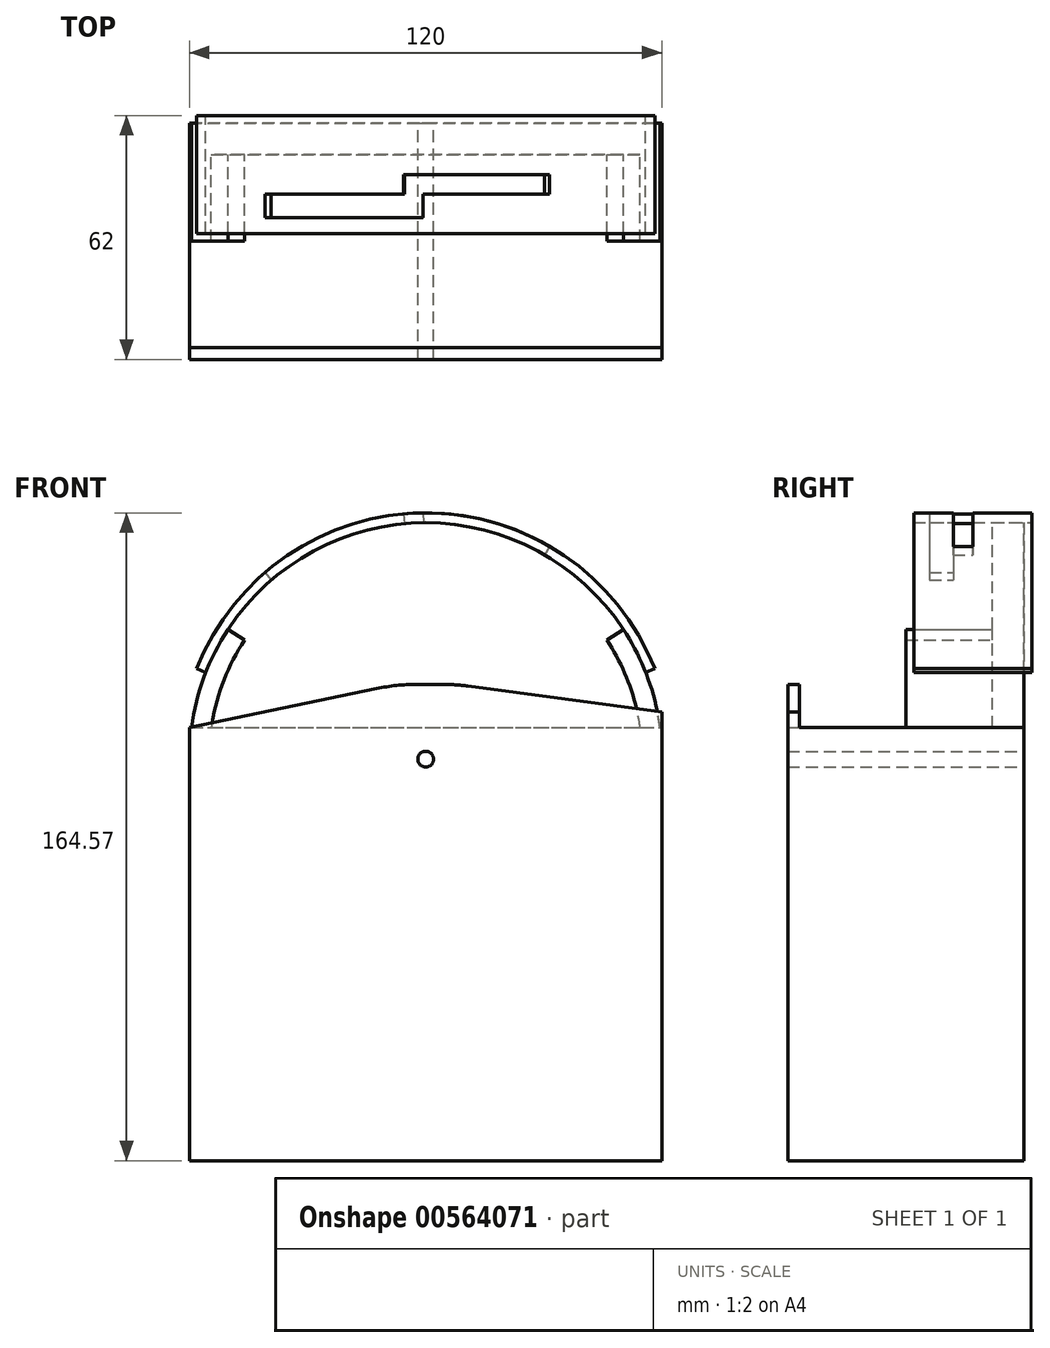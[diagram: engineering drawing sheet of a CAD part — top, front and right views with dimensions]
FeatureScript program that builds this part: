
annotation { "Feature Type Name" : "Feature", "Feature Type Description" : "" }
export const myFeature = defineFeature(function(context is Context, id is Id, definition is map)
    precondition{}
    {
        {
            var Q0;
            Q0=qCreatedBy(makeId("Front.planeOp"),FACE);
            var sketch = newSketch(context, id + "F0", { "sketchPlane" : qUnion([Q0])});
            skLineSegment(sketch, "E0.bottom", {"start": v(-60, 8) * mm, "end": v(60, 8) * mm});
            skLineSegment(sketch, "E0.top", {"start": v(-60, -102) * mm, "end": v(60, -102) * mm});
            skLineSegment(sketch, "E0.left", {"start": v(-60, 8) * mm, "end": v(-60, -102) * mm});
            skLineSegment(sketch, "E0.right", {"start": v(60, 8) * mm, "end": v(60, -102) * mm});
            skLineSegment(sketch, "E1", {"start": v(-60, 3) * mm, "end": v(60, 3) * mm});
            skArc(sketch, "E2", {"start": v(60.07, 0) * mm, "mid": v(0, 60.07) * mm, "end": v(-60.07, 0) * mm});
            skArc(sketch, "E3", {"start": v(55.07, 0) * mm, "mid": v(0, 55.07) * mm, "end": v(-55.07, 0) * mm});
            skArc(sketch, "E4", {"start": v(62.57, 0) * mm, "mid": v(0, 62.57) * mm, "end": v(-62.57, 0) * mm});
            skLineSegment(sketch, "E5", {"start": v(0, 0) * mm, "end": v(-50.2, 33) * mm, "construction": true});
            skLineSegment(sketch, "E6", {"start": v(0, 0) * mm, "end": v(50.2, 33) * mm, "construction": true});
            skLineSegment(sketch, "E7", {"start": v(0, 0) * mm, "end": v(-58.2, 23) * mm, "construction": true});
            skLineSegment(sketch, "E8", {"start": v(0, 0) * mm, "end": v(58.2, 23) * mm, "construction": true});
            skLineSegment(sketch, "E9", {"start": v(0, 0) * mm, "end": v(-40.86, 47.39) * mm, "construction": true});
            skLineSegment(sketch, "E10", {"start": v(0, 0) * mm, "end": v(-5.63, 62.32) * mm, "construction": true});
            skLineSegment(sketch, "E11", {"start": v(0, 0) * mm, "end": v(-0.63, 62.57) * mm, "construction": true});
            skLineSegment(sketch, "E12", {"start": v(0, 0) * mm, "end": v(31.46, 54.09) * mm, "construction": true});
            skLineSegment(sketch, "E13", {"start": v(-58.2, 23) * mm, "end": v(-55.87, 22.08) * mm});
            skLineSegment(sketch, "E14", {"start": v(-50.2, 33) * mm, "end": v(-46.02, 30.25) * mm});
            skLineSegment(sketch, "E15", {"start": v(-40.86, 47.39) * mm, "end": v(-39.23, 45.5) * mm});
            skLineSegment(sketch, "E16", {"start": v(-5.63, 62.32) * mm, "end": v(-5.4, 59.83) * mm});
            skLineSegment(sketch, "E17", {"start": v(-0.63, 62.57) * mm, "end": v(-0.6, 60.07) * mm});
            skLineSegment(sketch, "E18", {"start": v(31.46, 54.09) * mm, "end": v(30.2, 51.93) * mm});
            skLineSegment(sketch, "E19", {"start": v(58.2, 23) * mm, "end": v(55.87, 22.08) * mm});
            skLineSegment(sketch, "E20", {"start": v(50.2, 33) * mm, "end": v(46.02, 30.25) * mm});
            skLineSegment(sketch, "E21", {"start": v(0, 0) * mm, "end": v(-40.78, 47.46) * mm, "construction": true});
            skLineSegment(sketch, "E22", {"start": v(0, 0) * mm, "end": v(-32.85, 53.26) * mm, "construction": true});
            skLineSegment(sketch, "E23", {"start": v(0, 0) * mm, "end": v(-27.84, 56.04) * mm, "construction": true});
            skLineSegment(sketch, "E24", {"start": v(0, 0) * mm, "end": v(-3.13, 62.5) * mm, "construction": true});
            skLineSegment(sketch, "E25", {"start": v(0, 0) * mm, "end": v(1.45, -28.96) * mm, "construction": true});
            skLineSegment(sketch, "E26", {"start": v(0, 0) * mm, "end": v(15.23, -24.68) * mm, "construction": true});
            skLineSegment(sketch, "E27", {"start": v(0, 0) * mm, "end": v(12.9, -25.97) * mm, "construction": true});
            skCircle(sketch, "E28", {"center": v(0, 0) * mm, "radius": 29 * mm, "construction": true});
            skSolve(sketch);
        }
        {
            var Q0;
            {var subQ6=sQuery(id+"F0.wireOp",EDGE,"E0.top");Q0=makeQuery(id+"F0.imprint","IMPRINT",FACE,{"disambiguationData":[TD([[makeQuery(id+"F0.imprint","IMPRINT",EDGE,{"derivedFrom":subQ6}),1.0]])]});}
            extrude(context, id + "F1", {"entities" : qUnion([Q0]), "depth" : 60 * mm, "offsetDistance" : 25 * mm});
        }
        {
            var Q0;
            {var subQ0=sQuery(id+"F0.wireOp",EDGE,"E3");var subQ1=sQuery(id+"F0.wireOp",EDGE,"E0.bottom");var subQ2=makeQuery(id+"F0.imprint","INTERSECT",VERTEX,{"disambiguationData":[OD(0.0)],"derivedFrom":[subQ1,subQ0]});Q0=makeQuery(id+"F0.imprint","IMPRINT",FACE,{"disambiguationData":[TD([[makeQuery(id+"F0.imprint","IMPRINT",EDGE,{"disambiguationData":[TD([[subQ2,-1.0]])],"derivedFrom":subQ1}),-1.0]])]});}
            var Q1;
            {var subQ0=sQuery(id+"F0.wireOp",EDGE,"E2");var subQ1=sQuery(id+"F0.wireOp",EDGE,"E0.bottom");var subQ2=makeQuery(id+"F0.imprint","INTERSECT",VERTEX,{"derivedFrom":[subQ1,subQ0]});Q1=makeQuery(id+"F0.imprint","IMPRINT",FACE,{"disambiguationData":[TD([[makeQuery(id+"F0.imprint","IMPRINT",EDGE,{"disambiguationData":[TD([[subQ2,1.0]])],"derivedFrom":subQ1}),-1.0]])]});}
            var Q2;
            {var subQ0=sQuery(id+"F0.wireOp",EDGE,"E0.right");var subQ1=sQuery(id+"F0.wireOp",EDGE,"E0.bottom");var subQ2=makeQuery(id+"F0.imprint","INTERSECT",VERTEX,{"derivedFrom":[subQ1,subQ0]});Q2=makeQuery(id+"F0.imprint","IMPRINT",FACE,{"disambiguationData":[TD([[makeQuery(id+"F0.imprint","IMPRINT",EDGE,{"disambiguationData":[TD([[subQ2,1.0]])],"derivedFrom":subQ1}),-1.0]])]});}
            var Q3;
            {var subQ0=sQuery(id+"F0.wireOp",EDGE,"E1");var subQ3=sQuery(id+"F0.wireOp",EDGE,"E3");var subQ5=makeQuery(id+"F0.imprint","INTERSECT",VERTEX,{"disambiguationData":[OD(0.0)],"derivedFrom":[subQ0,subQ3]});Q3=makeQuery(id+"F0.imprint","IMPRINT",FACE,{"disambiguationData":[TD([[makeQuery(id+"F0.imprint","IMPRINT",EDGE,{"disambiguationData":[TD([[subQ5,1.0]])],"derivedFrom":subQ3}),-1.0]])]});}
            var Q4;
            {var subQ0=sQuery(id+"F0.wireOp",EDGE,"E2");var subQ1=sQuery(id+"F0.wireOp",EDGE,"E0.bottom");var subQ2=makeQuery(id+"F0.imprint","INTERSECT",VERTEX,{"disambiguationData":[OD(1.0)],"derivedFrom":[subQ1,subQ0]});Q4=makeQuery(id+"F0.imprint","IMPRINT",FACE,{"disambiguationData":[TD([[makeQuery(id+"F0.imprint","IMPRINT",EDGE,{"disambiguationData":[TD([[subQ2,1.0]])],"derivedFrom":subQ1}),-1.0]])]});}
            extrude(context, id + "F2", {"entities" : qUnion([Q0, Q1, Q2, Q3, Q4]), "operationType" : NewBodyOperationType.ADD, "depth" : 60 * mm, "offsetDistance" : 25 * mm});
        }
        {
            var Q0;
            {var subQ0=sQuery(id+"F0.wireOp",EDGE,"E3");var subQ1=sQuery(id+"F0.wireOp",EDGE,"E0.bottom");var subQ2=makeQuery(id+"F0.imprint","INTERSECT",VERTEX,{"disambiguationData":[OD(0.0)],"derivedFrom":[subQ1,subQ0]});Q0=makeQuery(id+"F0.imprint","IMPRINT",FACE,{"disambiguationData":[TD([[makeQuery(id+"F0.imprint","IMPRINT",EDGE,{"disambiguationData":[TD([[subQ2,-1.0]])],"derivedFrom":subQ1}),-1.0]])]});}
            var Q1;
            {var subQ0=sQuery(id+"F0.wireOp",EDGE,"E2");var subQ1=sQuery(id+"F0.wireOp",EDGE,"E0.bottom");var subQ2=makeQuery(id+"F0.imprint","INTERSECT",VERTEX,{"derivedFrom":[subQ1,subQ0]});Q1=makeQuery(id+"F0.imprint","IMPRINT",FACE,{"disambiguationData":[TD([[makeQuery(id+"F0.imprint","IMPRINT",EDGE,{"disambiguationData":[TD([[subQ2,1.0]])],"derivedFrom":subQ1}),-1.0]])]});}
            var Q2;
            {var subQ0=sQuery(id+"F0.wireOp",EDGE,"E3");var subQ1=sQuery(id+"F0.wireOp",EDGE,"E0.bottom");var subQ2=makeQuery(id+"F0.imprint","INTERSECT",VERTEX,{"disambiguationData":[OD(0.0)],"derivedFrom":[subQ1,subQ0]});Q2=makeQuery(id+"F0.imprint","IMPRINT",FACE,{"disambiguationData":[TD([[makeQuery(id+"F0.imprint","IMPRINT",EDGE,{"disambiguationData":[TD([[subQ2,-1.0]])],"derivedFrom":subQ1}),1.0]])]});}
            var Q3;
            {var subQ2=sQuery(id+"F0.wireOp",EDGE,"E20");Q3=makeQuery(id+"F0.imprint","IMPRINT",FACE,{"disambiguationData":[TD([[makeQuery(id+"F0.imprint","IMPRINT",EDGE,{"derivedFrom":subQ2}),1.0]])]});}
            var Q4;
            {var subQ6=sQuery(id+"F0.wireOp",EDGE,"E14");Q4=makeQuery(id+"F0.imprint","IMPRINT",FACE,{"disambiguationData":[TD([[makeQuery(id+"F0.imprint","IMPRINT",EDGE,{"derivedFrom":subQ6}),1.0]])]});}
            var Q5;
            {var subQ0=sQuery(id+"F0.wireOp",EDGE,"E14");Q5=makeQuery(id+"F0.imprint","IMPRINT",FACE,{"disambiguationData":[TD([[makeQuery(id+"F0.imprint","IMPRINT",EDGE,{"derivedFrom":subQ0}),-1.0]])]});}
            var Q6;
            {var subQ0=sQuery(id+"F0.wireOp",EDGE,"E1");var subQ3=sQuery(id+"F0.wireOp",EDGE,"E3");var subQ5=makeQuery(id+"F0.imprint","INTERSECT",VERTEX,{"disambiguationData":[OD(0.0)],"derivedFrom":[subQ0,subQ3]});Q6=makeQuery(id+"F0.imprint","IMPRINT",FACE,{"disambiguationData":[TD([[makeQuery(id+"F0.imprint","IMPRINT",EDGE,{"disambiguationData":[TD([[subQ5,1.0]])],"derivedFrom":subQ3}),-1.0]])]});}
            var Q7;
            {var subQ0=sQuery(id+"F0.wireOp",EDGE,"E2");var subQ1=sQuery(id+"F0.wireOp",EDGE,"E0.bottom");var subQ2=makeQuery(id+"F0.imprint","INTERSECT",VERTEX,{"disambiguationData":[OD(1.0)],"derivedFrom":[subQ1,subQ0]});Q7=makeQuery(id+"F0.imprint","IMPRINT",FACE,{"disambiguationData":[TD([[makeQuery(id+"F0.imprint","IMPRINT",EDGE,{"disambiguationData":[TD([[subQ2,1.0]])],"derivedFrom":subQ1}),-1.0]])]});}
            extrude(context, id + "F3", {"entities" : qUnion([Q0, Q1, Q2, Q3, Q4, Q5, Q6, Q7]), "operationType" : NewBodyOperationType.ADD, "depth" : 8 * mm, "offsetDistance" : 25 * mm});
        }
        {
            var Q0;
            {var subQ0=sQuery(id+"F0.wireOp",EDGE,"E14");Q0=makeQuery(id+"F0.imprint","IMPRINT",FACE,{"disambiguationData":[TD([[makeQuery(id+"F0.imprint","IMPRINT",EDGE,{"derivedFrom":subQ0}),-1.0]])]});}
            var Q1;
            {var subQ2=sQuery(id+"F0.wireOp",EDGE,"E20");Q1=makeQuery(id+"F0.imprint","IMPRINT",FACE,{"disambiguationData":[TD([[makeQuery(id+"F0.imprint","IMPRINT",EDGE,{"derivedFrom":subQ2}),1.0]])]});}
            var Q2;
            {var subQ0=sQuery(id+"F0.wireOp",EDGE,"E2");var subQ1=sQuery(id+"F0.wireOp",EDGE,"E0.bottom");var subQ2=makeQuery(id+"F0.imprint","INTERSECT",VERTEX,{"derivedFrom":[subQ1,subQ0]});Q2=makeQuery(id+"F0.imprint","IMPRINT",FACE,{"disambiguationData":[TD([[makeQuery(id+"F0.imprint","IMPRINT",EDGE,{"disambiguationData":[TD([[subQ2,1.0]])],"derivedFrom":subQ1}),-1.0]])]});}
            var Q3;
            {var subQ0=sQuery(id+"F0.wireOp",EDGE,"E1");var subQ3=sQuery(id+"F0.wireOp",EDGE,"E3");var subQ5=makeQuery(id+"F0.imprint","INTERSECT",VERTEX,{"disambiguationData":[OD(0.0)],"derivedFrom":[subQ0,subQ3]});Q3=makeQuery(id+"F0.imprint","IMPRINT",FACE,{"disambiguationData":[TD([[makeQuery(id+"F0.imprint","IMPRINT",EDGE,{"disambiguationData":[TD([[subQ5,1.0]])],"derivedFrom":subQ3}),-1.0]])]});}
            var Q4;
            {var subQ0=sQuery(id+"F0.wireOp",EDGE,"E2");var subQ1=sQuery(id+"F0.wireOp",EDGE,"E0.bottom");var subQ2=makeQuery(id+"F0.imprint","INTERSECT",VERTEX,{"disambiguationData":[OD(1.0)],"derivedFrom":[subQ1,subQ0]});Q4=makeQuery(id+"F0.imprint","IMPRINT",FACE,{"disambiguationData":[TD([[makeQuery(id+"F0.imprint","IMPRINT",EDGE,{"disambiguationData":[TD([[subQ2,1.0]])],"derivedFrom":subQ1}),-1.0]])]});}
            extrude(context, id + "F4", {"entities" : qUnion([Q0, Q1, Q2, Q3, Q4]), "operationType" : NewBodyOperationType.ADD, "depth" : 30 * mm, "offsetDistance" : 25 * mm});
        }
        {
            var Q0;
            {var subQ0=sQuery(id+"F0.wireOp",EDGE,"E13");Q0=makeQuery(id+"F0.imprint","IMPRINT",FACE,{"disambiguationData":[TD([[makeQuery(id+"F0.imprint","IMPRINT",EDGE,{"derivedFrom":subQ0}),1.0]])]});}
            var Q1;
            {var subQ0=sQuery(id+"F0.wireOp",EDGE,"E15");Q1=makeQuery(id+"F0.imprint","IMPRINT",FACE,{"disambiguationData":[TD([[makeQuery(id+"F0.imprint","IMPRINT",EDGE,{"derivedFrom":subQ0}),1.0]])]});}
            var Q2;
            {var subQ0=sQuery(id+"F0.wireOp",EDGE,"E16");Q2=makeQuery(id+"F0.imprint","IMPRINT",FACE,{"disambiguationData":[TD([[makeQuery(id+"F0.imprint","IMPRINT",EDGE,{"derivedFrom":subQ0}),1.0]])]});}
            var Q3;
            {var subQ0=sQuery(id+"F0.wireOp",EDGE,"E17");Q3=makeQuery(id+"F0.imprint","IMPRINT",FACE,{"disambiguationData":[TD([[makeQuery(id+"F0.imprint","IMPRINT",EDGE,{"derivedFrom":subQ0}),1.0]])]});}
            var Q4;
            {var subQ0=sQuery(id+"F0.wireOp",EDGE,"E18");Q4=makeQuery(id+"F0.imprint","IMPRINT",FACE,{"disambiguationData":[TD([[makeQuery(id+"F0.imprint","IMPRINT",EDGE,{"derivedFrom":subQ0}),1.0]])]});}
            extrude(context, id + "F5", {"entities" : qUnion([Q0, Q1, Q2, Q3, Q4]), "depth" : 28 * mm, "offsetDistance" : 25 * mm, "hasSecondDirection" : true, "secondDirectionOppositeDirection" : true, "secondDirectionDepth" : 2 * mm});
        }
        {
            var Q0;
            {var subQ0=sQuery(id+"F0.wireOp",EDGE,"E17");Q0=makeQuery(id+"F0.imprint","IMPRINT",FACE,{"disambiguationData":[TD([[makeQuery(id+"F0.imprint","IMPRINT",EDGE,{"derivedFrom":subQ0}),1.0]])]});}
            var Q1;
            {var subQ0=sQuery(id+"F0.wireOp",EDGE,"E16");Q1=makeQuery(id+"F0.imprint","IMPRINT",FACE,{"disambiguationData":[TD([[makeQuery(id+"F0.imprint","IMPRINT",EDGE,{"derivedFrom":subQ0}),1.0]])]});}
            extrude(context, id + "F6", {"entities" : qUnion([Q0, Q1]), "operationType" : NewBodyOperationType.REMOVE, "depth" : 18 * mm, "offsetDistance" : 25 * mm, "hasSecondDirection" : true, "secondDirectionOppositeDirection" : false, "secondDirectionDepth" : 13 * mm});
        }
        {
            var Q0;
            {var subQ0=sQuery(id+"F0.wireOp",EDGE,"E16");Q0=makeQuery(id+"F0.imprint","IMPRINT",FACE,{"disambiguationData":[TD([[makeQuery(id+"F0.imprint","IMPRINT",EDGE,{"derivedFrom":subQ0}),1.0]])]});}
            var Q1;
            {var subQ0=sQuery(id+"F0.wireOp",EDGE,"E15");Q1=makeQuery(id+"F0.imprint","IMPRINT",FACE,{"disambiguationData":[TD([[makeQuery(id+"F0.imprint","IMPRINT",EDGE,{"derivedFrom":subQ0}),1.0]])]});}
            extrude(context, id + "F7", {"entities" : qUnion([Q0, Q1]), "operationType" : NewBodyOperationType.REMOVE, "depth" : 24 * mm, "offsetDistance" : 25 * mm, "hasSecondDirection" : true, "secondDirectionOppositeDirection" : false, "secondDirectionDepth" : 18 * mm});
        }
        {
            var Q0;
            Q0=sQuery(id+"F0.wireOp",VERTEX,"E8.start");
            var Q1;
            Q1=makeQuery(id+"F1.opExtrude","SWEPT_BODY",BODY,{"disambiguationData":[OSD([sQuery(id+"F0.wireOp",EDGE,"E0.top"),sQuery(id+"F0.wireOp",EDGE,"E0.left"),sQuery(id+"F0.wireOp",EDGE,"E0.right"),sQuery(id+"F0.wireOp",EDGE,"E1")])]});
            hole(context, id + "F8", {"style" : HoleStyle.SIMPLE, "endStyle" : HoleEndStyle.THROUGH, "oppositeDirection" : true, "holeDiameter" : 4 * mm, "majorDiameter" : 5 * mm, "isTappedThrough" : true, "tappedDepth" : 12 * mm, "tapClearance" : 3, "locations" : qUnion([Q0]), "scope" : qUnion([Q1])});
        }
        {
            var Q0;
            {var subQ0=sQuery(id+"F0.wireOp",EDGE,"E1");var subQ1=sQuery(id+"F0.wireOp",EDGE,"E0.right");var subQ2=sQuery(id+"F0.wireOp",EDGE,"E0.left");Q0=makeQuery(id+"F2.boolean.opBoolean","MERGE",FACE,{"derivedFrom":[makeQuery(id+"F1.opExtrude","CAP_FACE",FACE,{"disambiguationData":[OSD([sQuery(id+"F0.wireOp",EDGE,"E0.top"),subQ2,subQ1,subQ0])],"isStart":false}),makeQuery(id+"F2.opExtrude","CAP_FACE",FACE,{"disambiguationData":[OSD([sQuery(id+"F0.wireOp",EDGE,"E0.bottom"),subQ2,subQ1,subQ0])],"isStart":false})]});}
            var sketch = newSketch(context, id + "F9", { "sketchPlane" : qUnion([Q0])});
            skCircle(sketch, "E29", {"center": v(0, 0) * mm, "radius": 27.5 * mm, "construction": true});
            skLineSegment(sketch, "E30", {"start": v(-20, 18.87) * mm, "end": v(-20, 38.87) * mm, "construction": true});
            skLineSegment(sketch, "E31", {"start": v(-20, 38.87) * mm, "end": v(20, 38.87) * mm, "construction": true});
            skLineSegment(sketch, "E32", {"start": v(20, 38.87) * mm, "end": v(20, 18.87) * mm, "construction": true});
            skLineSegment(sketch, "E33", {"start": v(0, 0) * mm, "end": v(-67.7, -6.29) * mm, "construction": true});
            skSolve(sketch);
        }
        {
            var Q0;
            {var subQ3=sQuery(id+"F0.wireOp",EDGE,"E0.top");Q0=makeQuery(id+"F9.imprint","IMPRINT",FACE,{"disambiguationData":[TD([[makeQuery(id+"F9.imprint","IMPRINT",EDGE,{"derivedFrom":makeQuery(id+"F1.opExtrude","CAP_EDGE",EDGE,{"disambiguationData":[OSD([subQ3])],"isStart":false})}),1.0]])]});}
            var sketch = newSketch(context, id + "F10", { "sketchPlane" : qUnion([Q0])});
            skLineSegment(sketch, "E34.0", {"start": v(-60, 8) * mm, "end": v(60, 8) * mm});
            skLineSegment(sketch, "E35", {"start": v(-60, 8) * mm, "end": v(-12.53, 17.94) * mm});
            skLineSegment(sketch, "E36", {"start": v(60, 8) * mm, "end": v(60, 12) * mm});
            skLineSegment(sketch, "E37", {"start": v(60, 12) * mm, "end": v(10.75, 18.56) * mm});
            skLineSegment(sketch, "E38", {"start": v(-2.29, 19) * mm, "end": v(4.15, 19) * mm});
            skPoint(sketch, "E39.visualSharp", {"position": v(-7.46, 19) * mm});
            skArc(sketch, "E39.filletArc", {"start": v(-2.29, 19) * mm, "mid": v(-7.44, 18.73) * mm, "end": v(-12.53, 17.94) * mm});
            skPoint(sketch, "E40.visualSharp", {"position": v(7.46, 19) * mm});
            skArc(sketch, "E40.filletArc", {"start": v(10.75, 18.56) * mm, "mid": v(7.46, 18.9) * mm, "end": v(4.15, 19) * mm});
            skSolve(sketch);
        }
        {
            var Q0;
            Q0=makeQuery(id+"F10.imprint","IMPRINT",FACE,{"disambiguationData":[TD([[makeQuery(id+"F10.imprint","IMPRINT",EDGE,{"derivedFrom":sQuery(id+"F10.wireOp",EDGE,"E34.0")}),1.0]])]});
            extrude(context, id + "F11", {"entities" : qUnion([Q0]), "operationType" : NewBodyOperationType.ADD, "oppositeDirection" : true, "depth" : 3 * mm, "offsetDistance" : 25 * mm});
        }
    });
